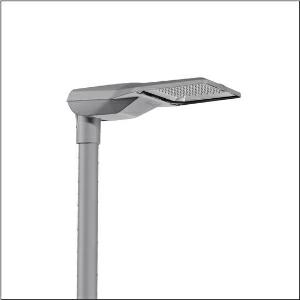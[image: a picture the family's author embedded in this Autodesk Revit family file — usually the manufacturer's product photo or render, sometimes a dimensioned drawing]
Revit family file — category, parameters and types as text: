
# Revit family: streetlight_sl_21_iq_midi___stw1_0a_5xe3e41g08nb_77a4
name_source: partatom
category: Lighting Fixtures
units: mm (PartAtom-declared; Revit-internal decimal feet)

## family parameters
Cut with Voids When Loaded = No
Host = Face
Light Source = No
Part Type = Normal
Room Calculation Point = No
Round Connector Dimension = Use Diameter
Shared = No

## types (1)
- --- (1 x LED, 24250 lm, 155.5 W, 4000K)
    Apparent Load = 155 VA
    CIE Flux Codes = 39 75 98 100 100
    Color Rendering = 70
    Color Temperature = 4000K
    Default Elevation = 1800 mm
    Description = Streetlight SL 21 iQ midi, mast luminaire, primary light control with lens, of PMMA, primary optical cover: cover, of toughened safety glass, transparent, light distribution: STW1.0a, light emission: direct distribution, primary light characteristic: asymmetric, installation type: post-top, side-entry, LED, High Power LED, rated luminous flux: 24.250lm, luminous efficacy: 156lm/W, light colour: 740, colour temperature: 4000K, control: Street-Remote, Auto-Match, Temp-Guard, Lumen-Switch, Night-Set, Smart-Wire, Light-Fading, Desk-Remote (wireless, voltage-free reading and setting of iQ features in the workshop via application-optimized NFC function/RFID function), optimised constant luminous flux control (CLO 2.0), pre-setting: linear dimming characteristic, mains connection: 230..240V, AC, 50/60Hz, start of lifetime: 156W, end of service life: 162W, reduction: 69W, luminaire housing, of diecast aluminium, powder-coated, Siteco® metallic grey (DB 702S), corrosivity category C5 mid according to DIN EN ISO 12944, please order mast flange separately, inclination adjustable: 0°, 5°, 10°, 15°, sealing non-destructively replaceable, multi-level sealing system, length: 644mm, width: 335mm, height: 110mm, mast flange for spigot size: 42mm (side-entry): 5XC10008XM4, 60/48mm (side-entry/post-top): 5XC10108XM2, 76/60mm (side-entry/post-top): 5XC10108XM1, protection rating (complete): IP66, insulation class (complete): insulation class II (safety insulation), certification: CE, ENEC, ENEC+, VDE, impact resistance: IK09, permissible operating ambient temperature for outdoor applications: -40..+50°C, standard-compliant lighting for roads and squares, packaging unit: 1 piece

Light Distribution: STW1.0a
    Height = 111 mm
    Lamp = 1 x LED
    Lamp Light Flux = 24250 lm
    Lamp Power = 155.5 W
    Lamp count = 1
    Length = 644 mm
    Luminous efficacy = 156 lm/W
    Manufacturer = Siteco
    ModVariant = No
    Model = 5XE3E41G08NB
    Number of Poles = 1
    OnlyDefault = Yes
    Power Factor = 1
    Product Name = Streetlight SL 21 iQ midi | STW1.0a
    Product group = mast luminaire | pylon top
    ProductGroupID = 6100
    Protection Class = Protection class II
    Protection Degree = IP 66
    RLX_Detail_Level = 1
    RLX_Emergency_Light_Flux = 0 lm
    RLX_Emergency_Type = 0
    RLX_Emergency_Type_DB = No
    RlxData = <blob elided: 90945 chars, md5=6ec6ab70>
    Socket = socket
    Standby Power = 0 W
    System Light Flux = 24250 lm
    System Power = 155 W
    Type Comments = factory setting: luminous flux: 100 % | dim-lin: 254 | 823 mA
    Type Image = l_1004298.jpg
    URL = http://relux.com
    VarID = @adj_140419
    Voltage = 0 V
    Weight = 0.00 kg
    Width = 336 mm

## geometry (parser evidence)
native form markers: Blend x4, Sweep x12
no freeform markers — native parametric forms only
